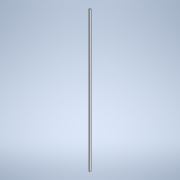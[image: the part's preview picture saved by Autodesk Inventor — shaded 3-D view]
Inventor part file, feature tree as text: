
AUTODESK INVENTOR PART (.ipt)
format: ipt  version: 2021 (Build 250183000, 183)  size: 93,696 bytes
history: native  units: mm
features: extrude x1, sketch x1
ambient origin geometry x8: Origin, YZ Plane, XZ Plane, XY Plane, X Axis, Y Axis, Z Axis, Center Point
bodies: Solid1 (feature_tree)
feature tree (2):
  extrude  "Extrusion1"  Depth=13.0mm
  sketch  "Sketch1"  dims[d0=13.0mm d1=13.0mm d2=1680.0mm d3=0.0mm]
